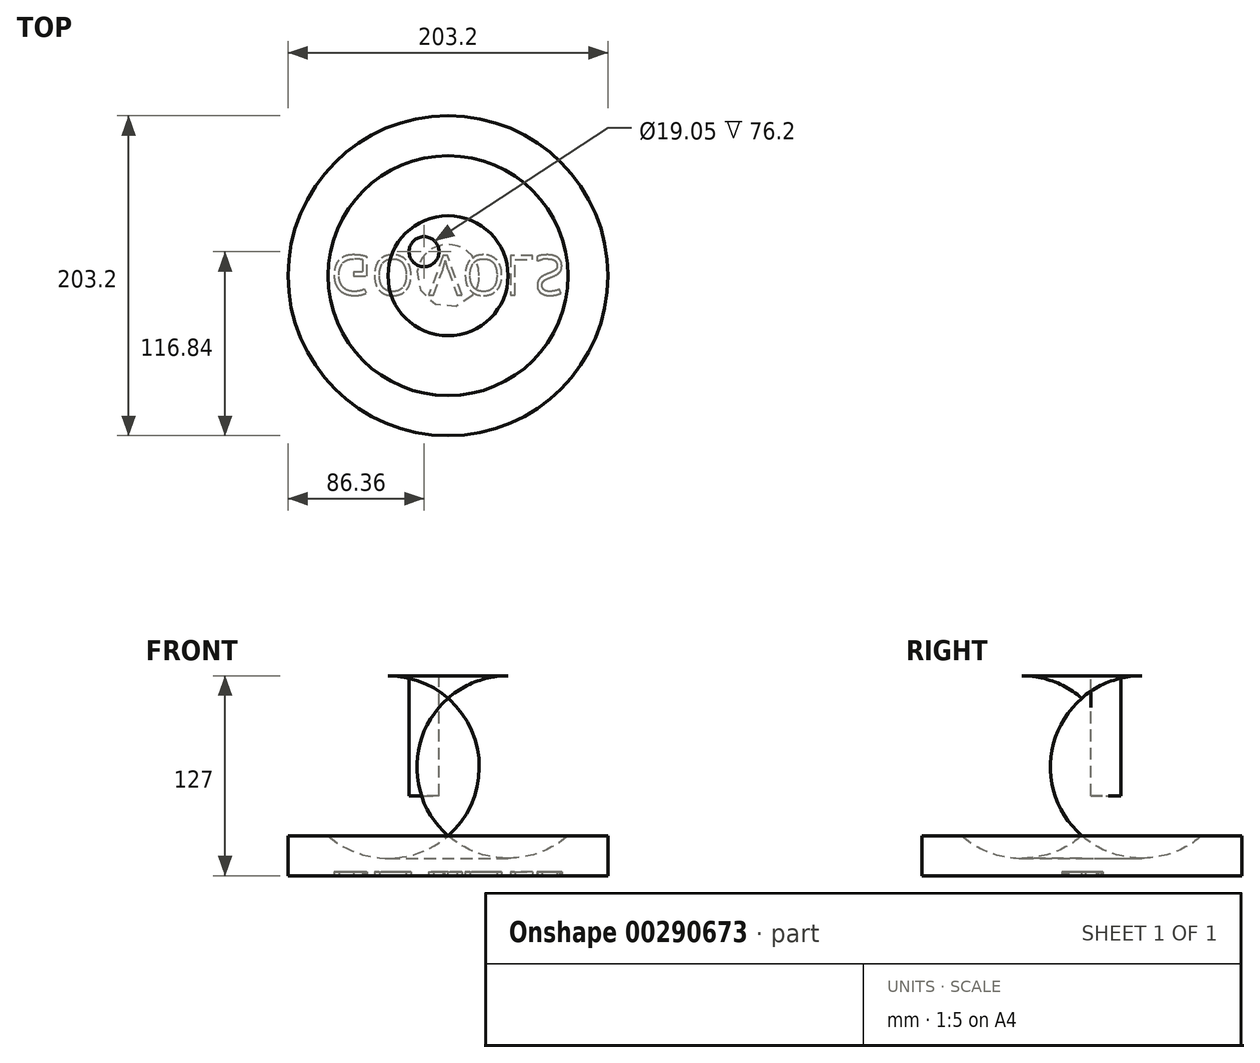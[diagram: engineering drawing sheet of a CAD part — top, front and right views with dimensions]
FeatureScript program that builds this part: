
annotation { "Feature Type Name" : "Feature", "Feature Type Description" : "" }
export const myFeature = defineFeature(function(context is Context, id is Id, definition is map)
    precondition{}
    {
        {
            var Q0;
            Q0=qCreatedBy(makeId("Right.planeOp"),FACE);
            var sketch = newSketch(context, id + "F0", { "sketchPlane" : qUnion([Q0])});
            skLineSegment(sketch, "E0", {"start": v(0, 0) * mm, "end": v(0, 127) * mm});
            skLineSegment(sketch, "E1", {"start": v(0, 127) * mm, "end": v(-38.1, 127) * mm});
            skLineSegment(sketch, "E2", {"start": v(0, 0) * mm, "end": v(-101.6, 0) * mm});
            skLineSegment(sketch, "E3", {"start": v(-101.6, 0) * mm, "end": v(-101.6, 25.4) * mm});
            skLineSegment(sketch, "E4", {"start": v(-101.6, 25.4) * mm, "end": v(-76.2, 25.4) * mm});
            skArc(sketch, "E5", {"start": v(-38.1, 127) * mm, "mid": v(-92.35, 89.4) * mm, "end": v(-76.2, 25.4) * mm});
            skSolve(sketch);
        }
        {
            var Q0;
            Q0=makeQuery(id+"F0.imprint","IMPRINT",FACE,{"disambiguationData":[TD([[makeQuery(id+"F0.imprint","IMPRINT",EDGE,{"derivedFrom":sQuery(id+"F0.wireOp",EDGE,"E0")}),1.0]])]});
            var Q1;
            Q1=sQuery(id+"F0.wireOp",EDGE,"E0");
            revolve(context, id + "F1", {"entities" : qUnion([Q0]), "axis" : qUnion([Q1]), "revolveType" : RevolveType.FULL});
        }
        {
            var Q0;
            Q0=makeQuery(id+"F1.opRevolve","SWEPT_FACE",FACE,{"disambiguationData":[OSD([sQuery(id+"F0.wireOp",EDGE,"E1")])]});
            var sketch = newSketch(context, id + "F2", { "sketchPlane" : qUnion([Q0])});
            skCircle(sketch, "E6", {"center": v(-15.24, 15.24) * mm, "radius": 9.53 * mm});
            skSolve(sketch);
        }
        {
            var Q0;
            Q0=makeQuery(id+"F2.imprint","IMPRINT",FACE,{"disambiguationData":[TD([[makeQuery(id+"F2.imprint","IMPRINT",EDGE,{"derivedFrom":sQuery(id+"F2.wireOp",EDGE,"E6")}),1.0]])]});
            extrude(context, id + "F3", {"entities" : qUnion([Q0]), "operationType" : NewBodyOperationType.REMOVE, "oppositeDirection" : true, "depth" : 76.2 * mm});
        }
        {
            var Q0;
            Q0=qCreatedBy(makeId("Right.planeOp"),FACE);
            var sketch = newSketch(context, id + "F4", { "sketchPlane" : qUnion([Q0])});
            skLineSegment(sketch, "E7", {"start": v(0, 204.43) * mm, "end": v(0, -144.34) * mm, "construction": true});
            skSolve(sketch);
        }
        {
            var Q0;
            Q0=makeQuery(id+"F1.opRevolve","SWEPT_FACE",FACE,{"disambiguationData":[OSD([sQuery(id+"F0.wireOp",EDGE,"E2")])]});
            var sketch = newSketch(context, id + "F5", { "sketchPlane" : qUnion([Q0])});
            skText(sketch, "E8", { "text": "GO VOLS", "fontName": "OpenSans-Regular.ttf"});
            const initialGuessF5  = {"E8": [-0.07453, -0.01296, 1, 0, 0.0254]};
            skSetInitialGuess(sketch, initialGuessF5);
            skSolve(sketch);
        }
        {
            var Q0;
            Q0 = qSketchRegion(id + "F5", true);
            extrude(context, id + "F6", {"entities" : qUnion([Q0]), "operationType" : NewBodyOperationType.REMOVE, "oppositeDirection" : true, "depth" : 2.54 * mm});
        }
    });
